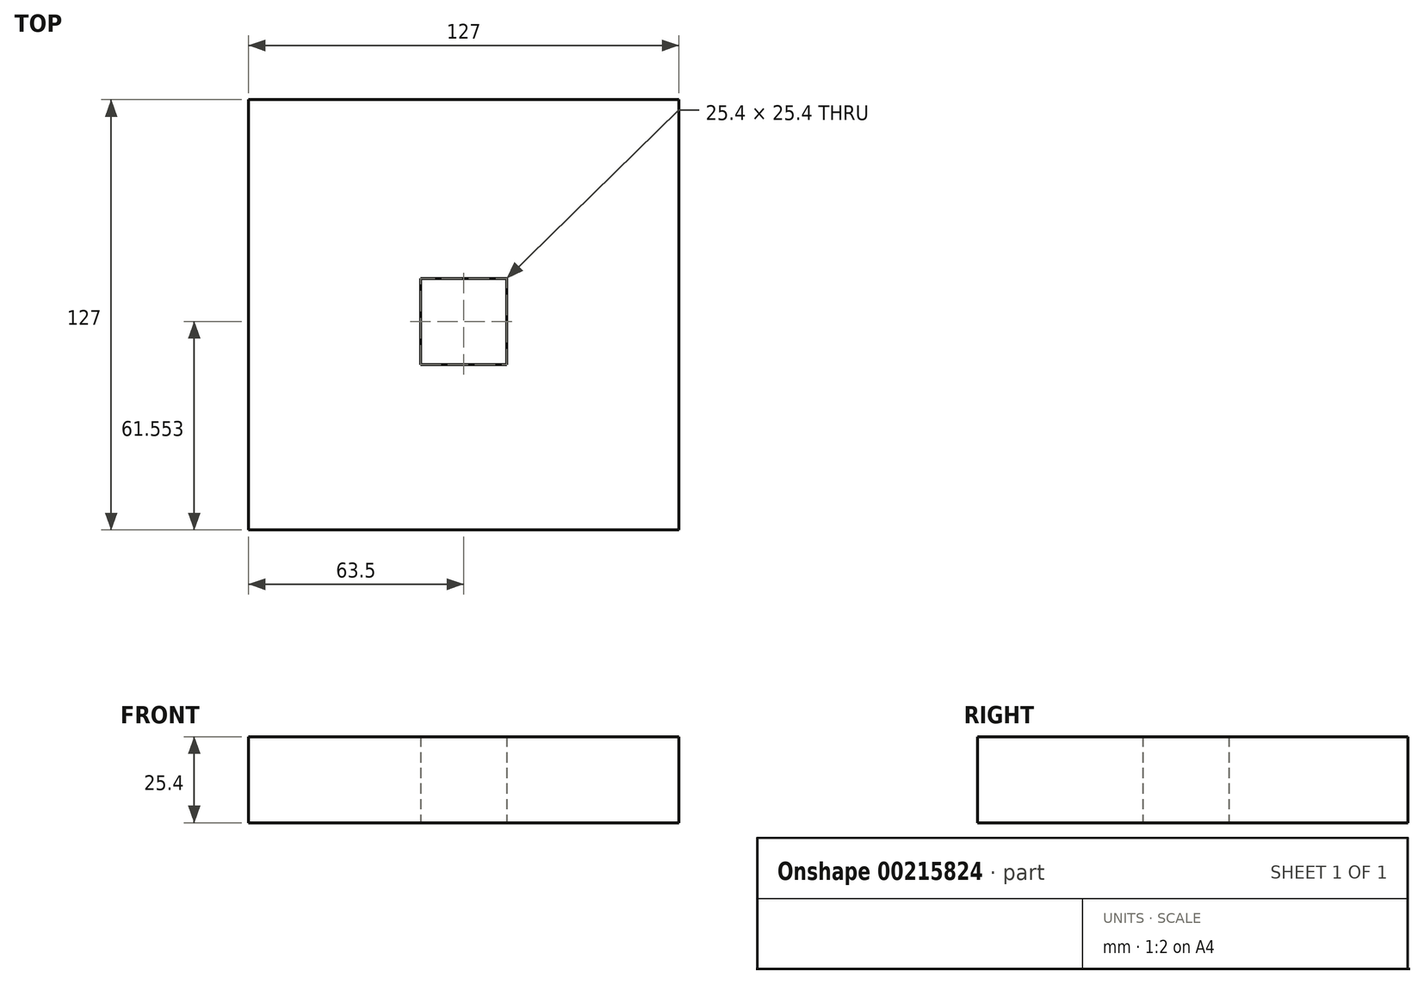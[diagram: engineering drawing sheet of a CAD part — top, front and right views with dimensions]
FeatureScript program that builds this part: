
annotation { "Feature Type Name" : "Feature", "Feature Type Description" : "" }
export const myFeature = defineFeature(function(context is Context, id is Id, definition is map)
    precondition{}
    {
        {
            var Q0;
            Q0=qCreatedBy(makeId("Top.planeOp"),FACE);
            var sketch = newSketch(context, id + "F0", { "sketchPlane" : qUnion([Q0])});
            skLineSegment(sketch, "E0.bottom", {"start": v(-63.5, 63.5) * mm, "end": v(63.5, 63.5) * mm});
            skLineSegment(sketch, "E0.top", {"start": v(-63.5, -63.5) * mm, "end": v(63.5, -63.5) * mm});
            skLineSegment(sketch, "E0.left", {"start": v(-63.5, 63.5) * mm, "end": v(-63.5, -63.5) * mm});
            skLineSegment(sketch, "E0.right", {"start": v(63.5, 63.5) * mm, "end": v(63.5, -63.5) * mm});
            skPoint(sketch, "E0.middle", {"position": v(0, 0) * mm});
            skLineSegment(sketch, "E1.bottom", {"start": v(0, 0) * mm, "end": v(0, 0) * mm});
            skLineSegment(sketch, "E2.bottom", {"start": v(12.7, -14.65) * mm, "end": v(-12.7, -14.65) * mm});
            skLineSegment(sketch, "E2.top", {"start": v(12.7, 10.75) * mm, "end": v(-12.7, 10.75) * mm});
            skLineSegment(sketch, "E2.left", {"start": v(12.7, -14.65) * mm, "end": v(12.7, 10.75) * mm});
            skLineSegment(sketch, "E2.right", {"start": v(-12.7, -14.65) * mm, "end": v(-12.7, 10.75) * mm});
            skPoint(sketch, "E2.middle", {"position": v(0, -1.95) * mm});
            skSolve(sketch);
        }
        {
            var Q0;
            Q0=makeQuery(id+"F0.imprint","IMPRINT",FACE,{"disambiguationData":[TD([[makeQuery(id+"F0.imprint","IMPRINT",EDGE,{"derivedFrom":sQuery(id+"F0.wireOp",EDGE,"E0.bottom")}),-1.0]])]});
            extrude(context, id + "F1", {"entities" : qUnion([Q0]), "depth" : 25.4 * mm});
        }
    });
